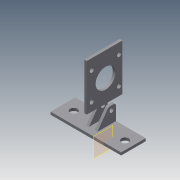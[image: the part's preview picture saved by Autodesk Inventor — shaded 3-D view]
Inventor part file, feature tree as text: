
AUTODESK INVENTOR PART (.ipt)
format: ipt  version: 2016 (Build 200138000, 138)  size: 260,608 bytes
history: native  units: in
note: dims shown in document units (in); Inventor stores cm internally (conversion verified against a paired STEP export)
features: extrude x7, sketch x7, chamfer x5, plane x1, fillet x1, draft x1
ambient origin geometry x8: Origin, YZ Plane, XZ Plane, XY Plane, X Axis, Y Axis, Z Axis, Center Point
bodies: Solid1 (feature_tree)
feature tree (22):
  extrude  "Extrusion1"  Depth=3.1496in
  plane  "Work Plane1"
  extrude  "Extrusion3"  Depth=0.3268in
  extrude  "Extrusion5"  Depth=0.1181in
  fillet  "Fillet1"  Radius=0.1181in
  extrude  "Extrusion6"  Depth=0.1181in TaperAngle=0.0deg
  draft  "FaceDraft1"
  chamfer  "Chamfer1"  Distance=0.7087in
  extrude  "Extrusion8"  Depth=0.125in
  extrude  "Extrusion9"  Depth=0.125in
  chamfer  "Chamfer2"  Distance=0.1875in
  extrude  "Extrusion10"  Depth=0.125in
  chamfer  "Chamfer3"  Distance=0.3937in
  chamfer  "Chamfer4"  Distance=0.2405in
  chamfer  "Chamfer5"  Distance=0.8858in
  sketch  "Sketch1"  dims[d0=1.1024in d1=3.1496in]
  sketch  "Sketch3"  dims[d2=0.3268in d3=0.3268in]
  sketch  "Sketch5"  dims[d4=0.5512in d5=0.5512in d6=0.1181in d7=0.0in]
  sketch  "Sketch6"  dims[d10=0.7874in d12=1.2205in d13=0.7874in d15=1.2205in d18=0.1181in d19=0.0in]
  sketch  "Sketch9"  dims[d22=0.1181in]
  sketch  "Sketch10"  dims[d23=0.1181in]
  sketch  "Sketch11"  dims[d24=0.26in d25=0.7087in d26=0.0in d27=0.9843in d28=0.125in d29=0.1875in d30=0.2in d31=0.3937in d32=0.0in d33=0.2405in d34=0.8858in d35=0.6102in d36=0.6102in d40=0.25in d41=0.25in d42=0.25in d43=0.25in d44=0.2in d45=0.125in d46=45.0deg d47=0.188in d48=0.2in d49=0.25in d50=0.0in d52=0.2992in d53=0.1181in d54=0.0in d55=0.05in d56=0.125in d57=45.0deg d58=0.1181in d59=0.0in d60=0.05in d61=0.125in d62=45.0deg d63=0.3in d64=0.125in d65=45.0deg d66=0.3in d67=0.125in d68=45.0deg]
